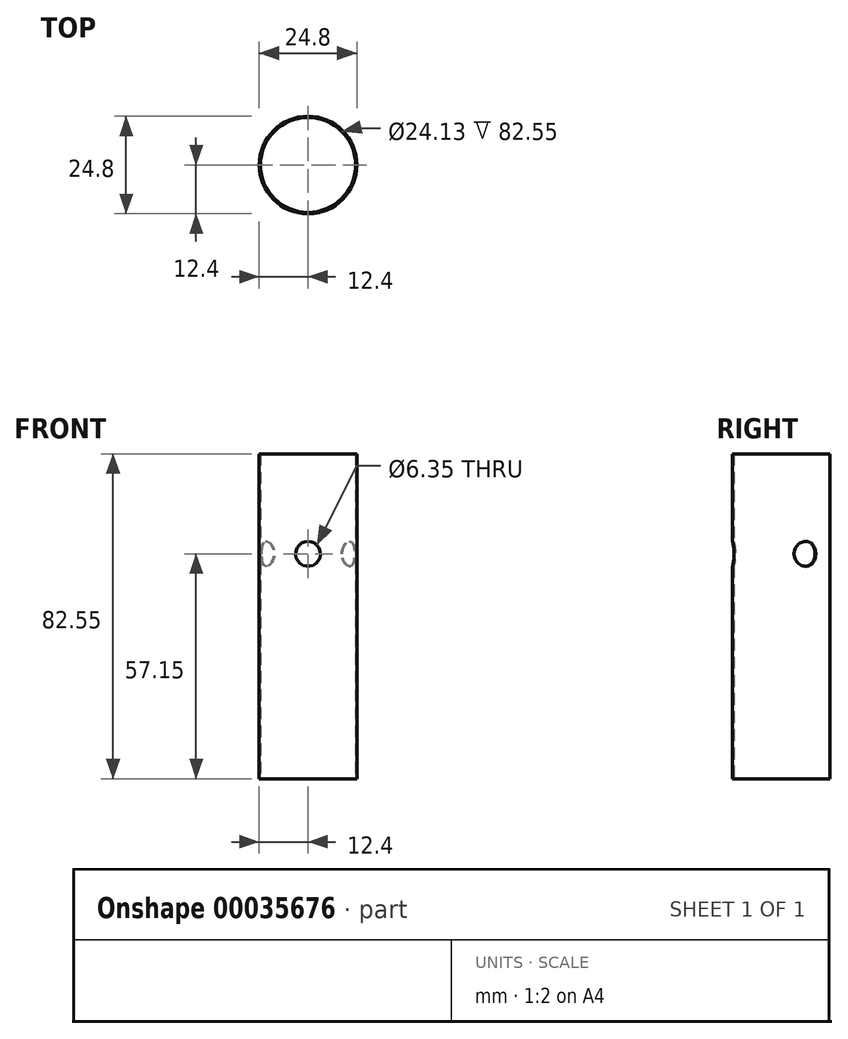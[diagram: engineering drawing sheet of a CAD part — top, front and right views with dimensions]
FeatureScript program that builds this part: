
annotation { "Feature Type Name" : "Feature", "Feature Type Description" : "" }
export const myFeature = defineFeature(function(context is Context, id is Id, definition is map)
    precondition{}
    {
        {
            var Q0;
            Q0=qCreatedBy(makeId("Front.planeOp"),FACE);
            var sketch = newSketch(context, id + "F0", { "sketchPlane" : qUnion([Q0])});
            skLineSegment(sketch, "E0", {"start": v(0, 0) * mm, "end": v(0, 82.55) * mm});
            skLineSegment(sketch, "E1", {"start": v(0, 82.55) * mm, "end": v(12.06, 82.55) * mm});
            skLineSegment(sketch, "E2", {"start": v(12.06, 82.55) * mm, "end": v(12.06, 0) * mm});
            skLineSegment(sketch, "E3", {"start": v(12.06, 0) * mm, "end": v(0, 0) * mm});
            skLineSegment(sketch, "E4", {"start": v(12.06, 0) * mm, "end": v(12.4, 0) * mm});
            skLineSegment(sketch, "E5", {"start": v(12.4, 0) * mm, "end": v(12.4, 82.55) * mm});
            skLineSegment(sketch, "E6", {"start": v(12.4, 82.55) * mm, "end": v(12.06, 82.55) * mm});
            skSolve(sketch);
        }
        {
            var Q0;
            Q0=makeQuery(id+"F0.imprint","IMPRINT",FACE,{"disambiguationData":[TD([[makeQuery(id+"F0.imprint","IMPRINT",EDGE,{"derivedFrom":sQuery(id+"F0.wireOp",EDGE,"E2")}),1.0]])]});
            var Q1;
            Q1=sQuery(id+"F0.wireOp",EDGE,"E0");
            revolve(context, id + "F1", {"entities" : qUnion([Q0]), "axis" : qUnion([Q1]), "revolveType" : RevolveType.FULL});
        }
        {
            var Q0;
            Q0=qCreatedBy(makeId("Front.planeOp"),FACE);
            var sketch = newSketch(context, id + "F2", { "sketchPlane" : qUnion([Q0])});
            skLineSegment(sketch, "E7", {"start": v(0, 0) * mm, "end": v(0, 82.55) * mm});
            skCircle(sketch, "E8", {"center": v(0, 57.15) * mm, "radius": 3.18 * mm});
            skSolve(sketch);
        }
        {
            var Q0;
            Q0 = qSketchRegion(id + "F2", true);
            extrude(context, id + "F3", {"entities" : qUnion([Q0]), "operationType" : NewBodyOperationType.REMOVE, "endBound" : BoundingType.THROUGH_ALL, "depth" : 25.4 * mm});
        }
        {
            var Q0;
            Q0=qCreatedBy(makeId("Top.planeOp"),FACE);
            var sketch = newSketch(context, id + "F4", { "sketchPlane" : qUnion([Q0])});
            skCircle(sketch, "E9.0", {"center": v(0, 0) * mm, "radius": 12.4 * mm});
            skLineSegment(sketch, "E10", {"start": v(0, 0) * mm, "end": v(0, 12.4) * mm});
            skLineSegment(sketch, "E11", {"start": v(0, 0) * mm, "end": v(0, -12.4) * mm});
            skLineSegment(sketch, "E12", {"start": v(0, 0) * mm, "end": v(10.73, -6.2) * mm});
            skLineSegment(sketch, "E13.MirrorCS", {"start": v(0, 0) * mm, "end": v(-10.73, -6.2) * mm});
            skLineSegment(sketch, "E14.MirrorCS", {"start": v(0, 0) * mm, "end": v(10.73, 6.2) * mm});
            skLineSegment(sketch, "E15.MirrorCS", {"start": v(0, 0) * mm, "end": v(-10.73, 6.2) * mm});
            skSolve(sketch);
        }
        {
            var Q0;
            Q0=sQuery(id+"F4.wireOp",EDGE,"E14.MirrorCS");
            var Q1;
            Q1=sQuery(id+"F4.wireOp",VERTEX,"E14.MirrorCS.end");
            cPlane(context, id + "F5", {"entities" : qUnion([Q0, Q1]), "cplaneType" : CPlaneType.LINE_POINT, "offset" : 152.4 * mm, "width" : 152.4 * mm, "height" : 152.4 * mm});
        }
        {
            var Q0;
            Q0=qCreatedBy(id+"F5.planeOp",FACE);
            var sketch = newSketch(context, id + "F6", { "sketchPlane" : qUnion([Q0])});
            skLineSegment(sketch, "E16", {"start": v(0, 0) * mm, "end": v(0, 82.55) * mm});
            skCircle(sketch, "E17", {"center": v(0, 57.15) * mm, "radius": 3.18 * mm});
            skSolve(sketch);
        }
        {
            var Q0;
            Q0 = qSketchRegion(id + "F6", true);
            var Q1;
            Q1=makeQuery(id+"F1.opRevolve","SWEPT_FACE",FACE,{"disambiguationData":[OSD([sQuery(id+"F0.wireOp",EDGE,"E2")])]});
            extrude(context, id + "F7", {"entities" : qUnion([Q0]), "operationType" : NewBodyOperationType.REMOVE, "endBound" : BoundingType.UP_TO_SURFACE, "oppositeDirection" : true, "endBoundEntityFace" : qUnion([Q1]), "depth" : 25.4 * mm});
        }
        {
            var Q0;
            Q0=sQuery(id+"F4.wireOp",EDGE,"E15.MirrorCS");
            var Q1;
            Q1=sQuery(id+"F4.wireOp",VERTEX,"E15.MirrorCS.end");
            cPlane(context, id + "F8", {"entities" : qUnion([Q0, Q1]), "cplaneType" : CPlaneType.LINE_POINT, "offset" : 152.4 * mm, "width" : 152.4 * mm, "height" : 152.4 * mm});
        }
        {
            var Q0;
            Q0=qCreatedBy(id+"F8.planeOp",FACE);
            var sketch = newSketch(context, id + "F9", { "sketchPlane" : qUnion([Q0])});
            skLineSegment(sketch, "E18", {"start": v(0, 0) * mm, "end": v(0, 82.55) * mm});
            skCircle(sketch, "E19", {"center": v(0, 57.15) * mm, "radius": 3.18 * mm});
            skSolve(sketch);
        }
        {
            var Q0;
            Q0 = qSketchRegion(id + "F9", true);
            var Q1;
            Q1=makeQuery(id+"F1.opRevolve","SWEPT_FACE",FACE,{"disambiguationData":[OSD([sQuery(id+"F0.wireOp",EDGE,"E2")])]});
            extrude(context, id + "F10", {"entities" : qUnion([Q0]), "operationType" : NewBodyOperationType.REMOVE, "endBound" : BoundingType.UP_TO_SURFACE, "oppositeDirection" : true, "endBoundEntityFace" : qUnion([Q1]), "depth" : 25.4 * mm});
        }
    });
